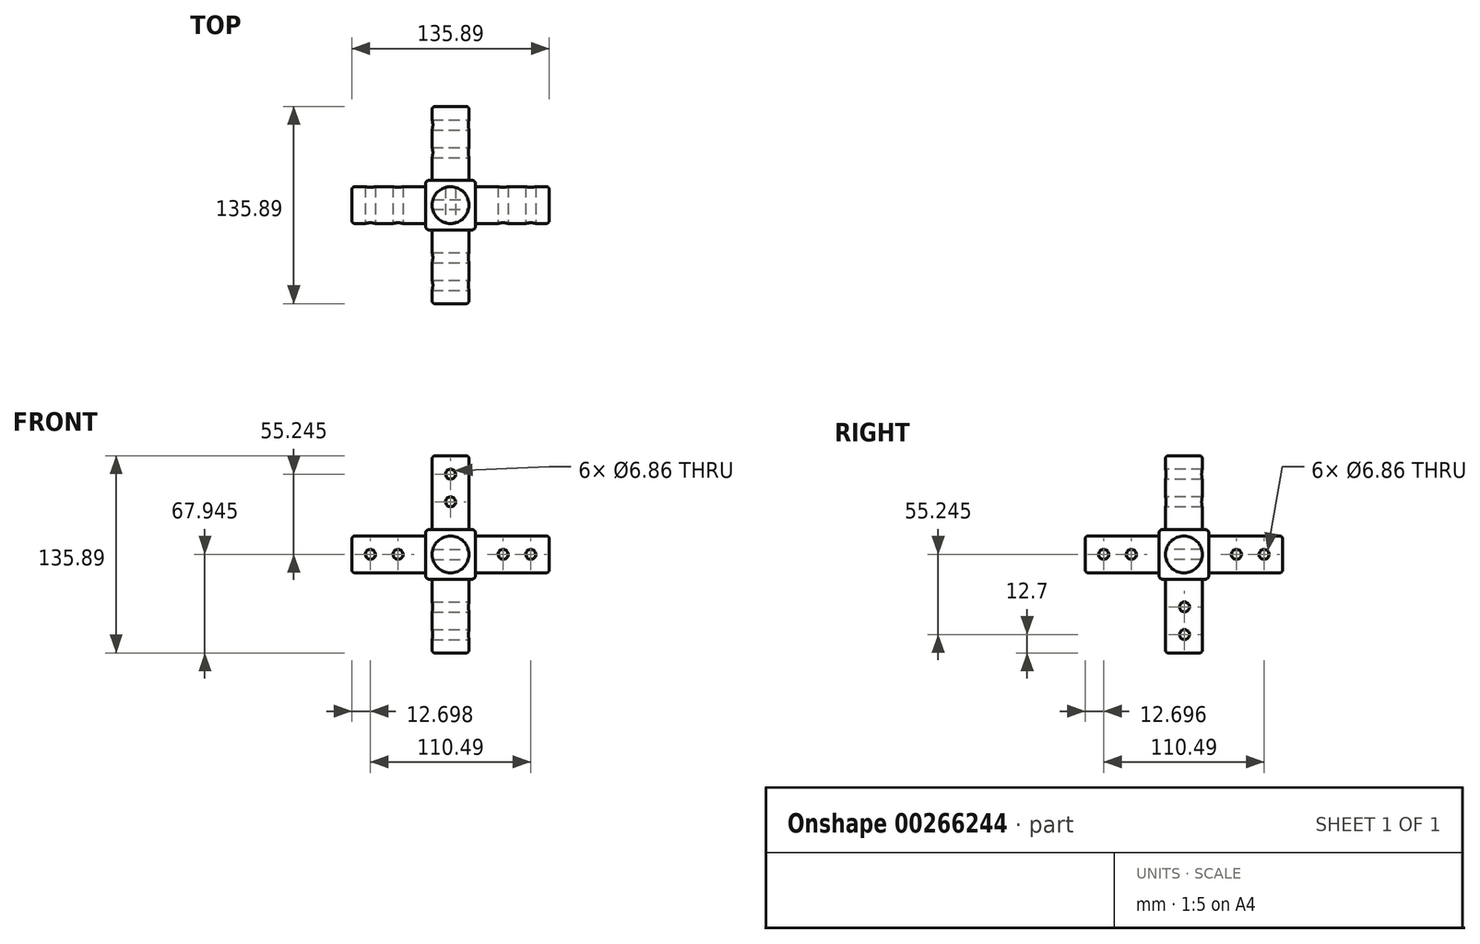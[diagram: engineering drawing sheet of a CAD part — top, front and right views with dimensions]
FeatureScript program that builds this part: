
annotation { "Feature Type Name" : "Feature", "Feature Type Description" : "" }
export const myFeature = defineFeature(function(context is Context, id is Id, definition is map)
    precondition{}
    {
        {
            var Q0;
            Q0=qCreatedBy(makeId("Top.planeOp"),FACE);
            var sketch = newSketch(context, id + "F0", { "sketchPlane" : qUnion([Q0])});
            skLineSegment(sketch, "E0.bottom", {"start": v(-13.47, 23.7) * mm, "end": v(20.82, 23.7) * mm});
            skLineSegment(sketch, "E0.top", {"start": v(-13.47, -10.58) * mm, "end": v(20.82, -10.58) * mm});
            skLineSegment(sketch, "E0.left", {"start": v(-13.47, 23.7) * mm, "end": v(-13.47, -10.58) * mm});
            skLineSegment(sketch, "E0.right", {"start": v(20.82, 23.7) * mm, "end": v(20.82, -10.58) * mm});
            skSolve(sketch);
        }
        {
            var Q0;
            Q0=qSketchRegion(id+"F0",true);
            extrude(context, id + "F1", {"entities" : qUnion([Q0]), "depth" : 34.3 * mm});
        }
        {
            var Q0;
            Q0=makeQuery(id+"F1.opExtrude","CAP_FACE",FACE,{"disambiguationData":[OSD([sQuery(id+"F0.wireOp",EDGE,"E0.bottom"),sQuery(id+"F0.wireOp",EDGE,"E0.top"),sQuery(id+"F0.wireOp",EDGE,"E0.left"),sQuery(id+"F0.wireOp",EDGE,"E0.right")])],"isStart":false});
            var sketch = newSketch(context, id + "F2", { "sketchPlane" : qUnion([Q0])});
            skCircle(sketch, "E1", {"center": v(3.68, 6.56) * mm, "radius": 12.7 * mm});
            skLineSegment(sketch, "E2", {"start": v(3.67, 23.7) * mm, "end": v(3.67, -12.79) * mm, "construction": true});
            skLineSegment(sketch, "E3", {"start": v(20.82, 6.56) * mm, "end": v(-13.47, 6.56) * mm, "construction": true});
            skSolve(sketch);
        }
        {
            var Q0;
            Q0=qSketchRegion(id+"F2",true);
            extrude(context, id + "F3", {"entities" : qUnion([Q0]), "operationType" : NewBodyOperationType.ADD, "depth" : 50.8 * mm});
        }
        {
            var Q0;
            Q0=makeQuery(id+"F1.opExtrude","SWEPT_FACE",FACE,{"disambiguationData":[OSD([sQuery(id+"F0.wireOp",EDGE,"E0.left")])]});
            var sketch = newSketch(context, id + "F4", { "sketchPlane" : qUnion([Q0])});
            skLineSegment(sketch, "E4", {"start": v(-23.7, 17.15) * mm, "end": v(13.45, 17.15) * mm, "construction": true});
            skLineSegment(sketch, "E5", {"start": v(-6.56, 0) * mm, "end": v(-6.56, 34.3) * mm, "construction": true});
            skCircle(sketch, "E6", {"center": v(-6.56, 17.15) * mm, "radius": 12.7 * mm});
            skSolve(sketch);
        }
        {
            var Q0;
            Q0=qSketchRegion(id+"F4",true);
            extrude(context, id + "F5", {"entities" : qUnion([Q0]), "operationType" : NewBodyOperationType.ADD, "depth" : 50.8 * mm});
        }
        {
            var Q0;
            Q0=makeQuery(id+"F1.opExtrude","SWEPT_FACE",FACE,{"disambiguationData":[OSD([sQuery(id+"F0.wireOp",EDGE,"E0.top")])]});
            var sketch = newSketch(context, id + "F6", { "sketchPlane" : qUnion([Q0])});
            skLineSegment(sketch, "E7", {"start": v(-13.47, 17.15) * mm, "end": v(24.43, 17.15) * mm, "construction": true});
            skLineSegment(sketch, "E8", {"start": v(3.67, 0) * mm, "end": v(3.67, 34.3) * mm, "construction": true});
            skCircle(sketch, "E9", {"center": v(3.67, 17.15) * mm, "radius": 12.7 * mm});
            skSolve(sketch);
        }
        {
            var Q0;
            Q0=qSketchRegion(id+"F6",true);
            extrude(context, id + "F7", {"entities" : qUnion([Q0]), "operationType" : NewBodyOperationType.ADD, "depth" : 50.8 * mm});
        }
        {
            var Q0;
            Q0=qCreatedBy(makeId("Front.planeOp"),FACE);
            var sketch = newSketch(context, id + "F8", { "sketchPlane" : qUnion([Q0])});
            skCircle(sketch, "E10", {"center": v(3.67, 53.34) * mm, "radius": 3.43 * mm});
            skCircle(sketch, "E11", {"center": v(3.67, 72.4) * mm, "radius": 3.43 * mm});
            skSolve(sketch);
        }
        {
            var Q0;
            Q0=qSketchRegion(id+"F8",true);
            extrude(context, id + "F9", {"entities" : qUnion([Q0]), "operationType" : NewBodyOperationType.REMOVE, "endBound" : BoundingType.SYMMETRIC, "oppositeDirection" : true, "depth" : 50.8 * mm});
        }
        {
            var Q0;
            Q0=qCreatedBy(makeId("Right.planeOp"),FACE);
            var sketch = newSketch(context, id + "F10", { "sketchPlane" : qUnion([Q0])});
            skCircle(sketch, "E12", {"center": v(-29.63, 17.15) * mm, "radius": 3.43 * mm});
            skCircle(sketch, "E13", {"center": v(-48.68, 17.15) * mm, "radius": 3.43 * mm});
            skSolve(sketch);
        }
        {
            var Q0;
            Q0=qSketchRegion(id+"F10",true);
            extrude(context, id + "F11", {"entities" : qUnion([Q0]), "operationType" : NewBodyOperationType.REMOVE, "endBound" : BoundingType.SYMMETRIC, "oppositeDirection" : true, "depth" : 50.8 * mm});
        }
        {
            var Q0;
            Q0=qCreatedBy(makeId("Front.planeOp"),FACE);
            var sketch = newSketch(context, id + "F12", { "sketchPlane" : qUnion([Q0])});
            skCircle(sketch, "E14", {"center": v(-51.57, 17.15) * mm, "radius": 3.43 * mm});
            skCircle(sketch, "E15", {"center": v(-32.52, 17.15) * mm, "radius": 3.43 * mm});
            skSolve(sketch);
        }
        {
            var Q0;
            Q0=qSketchRegion(id+"F12",true);
            extrude(context, id + "F13", {"entities" : qUnion([Q0]), "operationType" : NewBodyOperationType.REMOVE, "endBound" : BoundingType.SYMMETRIC, "oppositeDirection" : true, "depth" : 50.8 * mm});
        }
        {
            var Q0;
            Q0=makeQuery(id+"F1.opExtrude","SWEPT_EDGE",EDGE,{"disambiguationData":[OSD([sQuery(id+"F0.wireOp",EDGE,"E0.bottom"),sQuery(id+"F0.wireOp",EDGE,"E0.right")])]});
            var Q1;
            Q1=makeQuery(id+"F1.opExtrude","CAP_EDGE",EDGE,{"disambiguationData":[OSD([sQuery(id+"F0.wireOp",EDGE,"E0.right")])],"isStart":false});
            var Q2;
            Q2=makeQuery(id+"F1.opExtrude","SWEPT_EDGE",EDGE,{"disambiguationData":[OSD([sQuery(id+"F0.wireOp",EDGE,"E0.top"),sQuery(id+"F0.wireOp",EDGE,"E0.right")])]});
            var Q3;
            Q3=makeQuery(id+"F1.opExtrude","CAP_EDGE",EDGE,{"disambiguationData":[OSD([sQuery(id+"F0.wireOp",EDGE,"E0.right")])],"isStart":true});
            var Q4;
            Q4=makeQuery(id+"F1.opExtrude","CAP_EDGE",EDGE,{"disambiguationData":[OSD([sQuery(id+"F0.wireOp",EDGE,"E0.bottom")])],"isStart":true});
            var Q5;
            Q5=makeQuery(id+"F1.opExtrude","CAP_EDGE",EDGE,{"disambiguationData":[OSD([sQuery(id+"F0.wireOp",EDGE,"E0.bottom")])],"isStart":false});
            var Q6;
            Q6=makeQuery(id+"F1.opExtrude","SWEPT_EDGE",EDGE,{"disambiguationData":[OSD([sQuery(id+"F0.wireOp",EDGE,"E0.bottom"),sQuery(id+"F0.wireOp",EDGE,"E0.left")])]});
            var Q7;
            Q7=makeQuery(id+"F1.opExtrude","CAP_EDGE",EDGE,{"disambiguationData":[OSD([sQuery(id+"F0.wireOp",EDGE,"E0.left")])],"isStart":true});
            var Q8;
            Q8=makeQuery(id+"F1.opExtrude","CAP_EDGE",EDGE,{"disambiguationData":[OSD([sQuery(id+"F0.wireOp",EDGE,"E0.top")])],"isStart":true});
            var Q9;
            Q9=makeQuery(id+"F1.opExtrude","CAP_EDGE",EDGE,{"disambiguationData":[OSD([sQuery(id+"F0.wireOp",EDGE,"E0.left")])],"isStart":false});
            var Q10;
            Q10=makeQuery(id+"F1.opExtrude","SWEPT_EDGE",EDGE,{"disambiguationData":[OSD([sQuery(id+"F0.wireOp",EDGE,"E0.top"),sQuery(id+"F0.wireOp",EDGE,"E0.left")])]});
            var Q11;
            Q11=makeQuery(id+"F1.opExtrude","CAP_EDGE",EDGE,{"disambiguationData":[OSD([sQuery(id+"F0.wireOp",EDGE,"E0.top")])],"isStart":false});
            fillet(context, id + "F14", {"entities" : qUnion([Q0, Q1, Q2, Q3, Q4, Q5, Q6, Q7, Q8, Q9, Q10, Q11]), "radius" : 2.54 * mm, "tangentPropagation" : true, "allowEdgeOverflow" : false});
        }
        {
            var Q0;
            Q0=makeQuery(id+"F1.opExtrude","SWEPT_FACE",FACE,{"disambiguationData":[OSD([sQuery(id+"F0.wireOp",EDGE,"E0.bottom")])]});
            var sketch = newSketch(context, id + "F15", { "sketchPlane" : qUnion([Q0])});
            skLineSegment(sketch, "E16", {"start": v(-18.28, 17.15) * mm, "end": v(4.82, 17.15) * mm, "construction": true});
            skPoint(sketch, "E16.endSnap0", {"position": v(-18.28, 17.15) * mm});
            skLineSegment(sketch, "E17", {"start": v(-3.67, 31.75) * mm, "end": v(-3.67, 14.65) * mm, "construction": true});
            skCircle(sketch, "E18", {"center": v(-3.67, 17.15) * mm, "radius": 12.7 * mm});
            skSolve(sketch);
        }
        {
            var Q0;
            Q0=qSketchRegion(id+"F15",true);
            extrude(context, id + "F16", {"entities" : qUnion([Q0]), "operationType" : NewBodyOperationType.ADD, "depth" : 50.8 * mm});
        }
        {
            var Q0;
            Q0=qCreatedBy(makeId("Right.planeOp"),FACE);
            var sketch = newSketch(context, id + "F17", { "sketchPlane" : qUnion([Q0])});
            skCircle(sketch, "E19", {"center": v(42.76, 17.15) * mm, "radius": 3.43 * mm});
            skCircle(sketch, "E20", {"center": v(61.8, 17.15) * mm, "radius": 3.43 * mm});
            skSolve(sketch);
        }
        {
            var Q0;
            Q0=qSketchRegion(id+"F17",true);
            extrude(context, id + "F18", {"entities" : qUnion([Q0]), "operationType" : NewBodyOperationType.REMOVE, "endBound" : BoundingType.SYMMETRIC, "oppositeDirection" : true, "depth" : 50.8 * mm});
        }
        {
            var Q0;
            Q0=makeQuery(id+"F1.opExtrude","SWEPT_FACE",FACE,{"disambiguationData":[OSD([sQuery(id+"F0.wireOp",EDGE,"E0.right")])]});
            var sketch = newSketch(context, id + "F19", { "sketchPlane" : qUnion([Q0])});
            skCircle(sketch, "E21", {"center": v(6.56, 17.14) * mm, "radius": 12.7 * mm});
            skLineSegment(sketch, "E22", {"start": v(-8.04, 17.15) * mm, "end": v(28.63, 17.15) * mm, "construction": true});
            skLineSegment(sketch, "E23", {"start": v(6.56, 2.54) * mm, "end": v(6.56, 27.82) * mm, "construction": true});
            skSolve(sketch);
        }
        {
            var Q0;
            Q0=qSketchRegion(id+"F19",true);
            extrude(context, id + "F20", {"entities" : qUnion([Q0]), "operationType" : NewBodyOperationType.ADD, "depth" : 50.8 * mm});
        }
        {
            var Q0;
            Q0=qCreatedBy(makeId("Front.planeOp"),FACE);
            var sketch = newSketch(context, id + "F21", { "sketchPlane" : qUnion([Q0])});
            skCircle(sketch, "E24", {"center": v(58.92, 17.15) * mm, "radius": 3.43 * mm});
            skCircle(sketch, "E25", {"center": v(39.87, 17.15) * mm, "radius": 3.43 * mm});
            skSolve(sketch);
        }
        {
            var Q0;
            Q0=qSketchRegion(id+"F21",true);
            extrude(context, id + "F22", {"entities" : qUnion([Q0]), "operationType" : NewBodyOperationType.REMOVE, "endBound" : BoundingType.SYMMETRIC, "oppositeDirection" : true, "depth" : 50.8 * mm});
        }
        {
            var Q0;
            Q0=makeQuery(id+"F1.opExtrude","CAP_FACE",FACE,{"disambiguationData":[OSD([sQuery(id+"F0.wireOp",EDGE,"E0.bottom"),sQuery(id+"F0.wireOp",EDGE,"E0.top"),sQuery(id+"F0.wireOp",EDGE,"E0.left"),sQuery(id+"F0.wireOp",EDGE,"E0.right")])],"isStart":true});
            var sketch = newSketch(context, id + "F23", { "sketchPlane" : qUnion([Q0])});
            skCircle(sketch, "E26", {"center": v(3.67, -6.56) * mm, "radius": 12.7 * mm});
            skPoint(sketch, "E26.centerSnap0", {"position": v(3.67, -21.17) * mm});
            skPoint(sketch, "E26.centerSnap1", {"position": v(18.28, -6.56) * mm});
            skSolve(sketch);
        }
        {
            var Q0;
            Q0=qSketchRegion(id+"F23",true);
            extrude(context, id + "F24", {"entities" : qUnion([Q0]), "operationType" : NewBodyOperationType.ADD, "depth" : 50.8 * mm});
        }
        {
            var Q0;
            Q0=makeQuery(id+"F3.opExtrude","CAP_EDGE",EDGE,{"disambiguationData":[OSD([sQuery(id+"F2.wireOp",EDGE,"E1")])],"isStart":false});
            var Q1;
            Q1=makeQuery(id+"F7.opExtrude","CAP_EDGE",EDGE,{"disambiguationData":[OSD([sQuery(id+"F6.wireOp",EDGE,"E9")])],"isStart":false});
            var Q2;
            Q2=makeQuery(id+"F5.opExtrude","CAP_EDGE",EDGE,{"disambiguationData":[OSD([sQuery(id+"F4.wireOp",EDGE,"E6")])],"isStart":false});
            var Q3;
            Q3=makeQuery(id+"F16.opExtrude","CAP_EDGE",EDGE,{"disambiguationData":[OSD([sQuery(id+"F15.wireOp",EDGE,"E18")])],"isStart":false});
            var Q4;
            Q4=makeQuery(id+"F20.opExtrude","CAP_EDGE",EDGE,{"disambiguationData":[OSD([sQuery(id+"F19.wireOp",EDGE,"E21")])],"isStart":false});
            var Q5;
            Q5=makeQuery(id+"F24.opExtrude","CAP_EDGE",EDGE,{"disambiguationData":[OSD([sQuery(id+"F23.wireOp",EDGE,"E26")])],"isStart":false});
            fillet(context, id + "F25", {"entities" : qUnion([Q0, Q1, Q2, Q3, Q4, Q5]), "radius" : 2.03 * mm, "tangentPropagation" : true, "allowEdgeOverflow" : false});
        }
        {
            var Q0;
            Q0=qCreatedBy(makeId("Right.planeOp"),FACE);
            var sketch = newSketch(context, id + "F26", { "sketchPlane" : qUnion([Q0])});
            skCircle(sketch, "E27", {"center": v(7.01, -19.05) * mm, "radius": 3.43 * mm});
            skCircle(sketch, "E28", {"center": v(7.01, -38.1) * mm, "radius": 3.43 * mm});
            skSolve(sketch);
        }
        {
            var Q0;
            Q0=qSketchRegion(id+"F26",true);
            extrude(context, id + "F27", {"entities" : qUnion([Q0]), "operationType" : NewBodyOperationType.REMOVE, "endBound" : BoundingType.SYMMETRIC, "oppositeDirection" : true, "depth" : 50.8 * mm});
        }
    });
